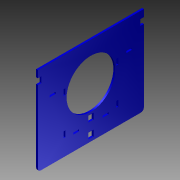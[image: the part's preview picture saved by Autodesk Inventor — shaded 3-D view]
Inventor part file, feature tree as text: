
AUTODESK INVENTOR PART (.ipt)
format: ipt  version: 2012 (Build 160160000, 160)  size: 176,640 bytes
history: native  units: mm
features: extrude x1, sketch x1
ambient origin geometry x8: Origin, YZ Plane, XZ Plane, XY Plane, X Axis, Y Axis, Z Axis, Center Point
feature tree (2):
  extrude  "Extrusion6"  Depth=6.0mm
  sketch  "Sketch2"  dims[d8=0.0mm d21=6.0mm d22=10.0mm d25=6.0mm d26=10.0mm d31=3.0mm d32=10.0mm d35=3.0mm d36=10.0mm d39=25.0mm d40=25.0mm d43=82.55mm d52=3.0mm d53=10.0mm d54=10.0mm d55=3.0mm d58=10.0mm d59=3.0mm d62=3.0mm d65=180.0mm d66=150.0mm d69=20.0mm d71=20.0mm d72=43.5mm d73=43.5mm d74=60.0mm d75=60.0mm d76=10.0mm d77=10.0mm d78=60.0mm d79=90.0mm d80=43.5mm d81=43.5mm d87=15.0mm d90=90.0mm d91=90.0mm d103=10.0mm d104=10.0mm d108=3.0mm d109=10.0mm d110=20.0mm d111=3.0mm d112=10.0mm d113=20.0mm d114=5.0mm d115=10.0mm d116=9.0mm d117=4.5mm d118=10.0mm d119=9.0mm d120=15.0mm d121=4.5mm d124=3.0mm d125=0.0mm d127=180.0mm d128=150.0mm d130=85.5mm d131=43.5mm d132=43.5mm d133=60.0mm d134=60.0mm d135=43.5mm d136=43.5mm d137=90.0deg d138=28.0mm d140=47.0mm d141=47.0mm]
